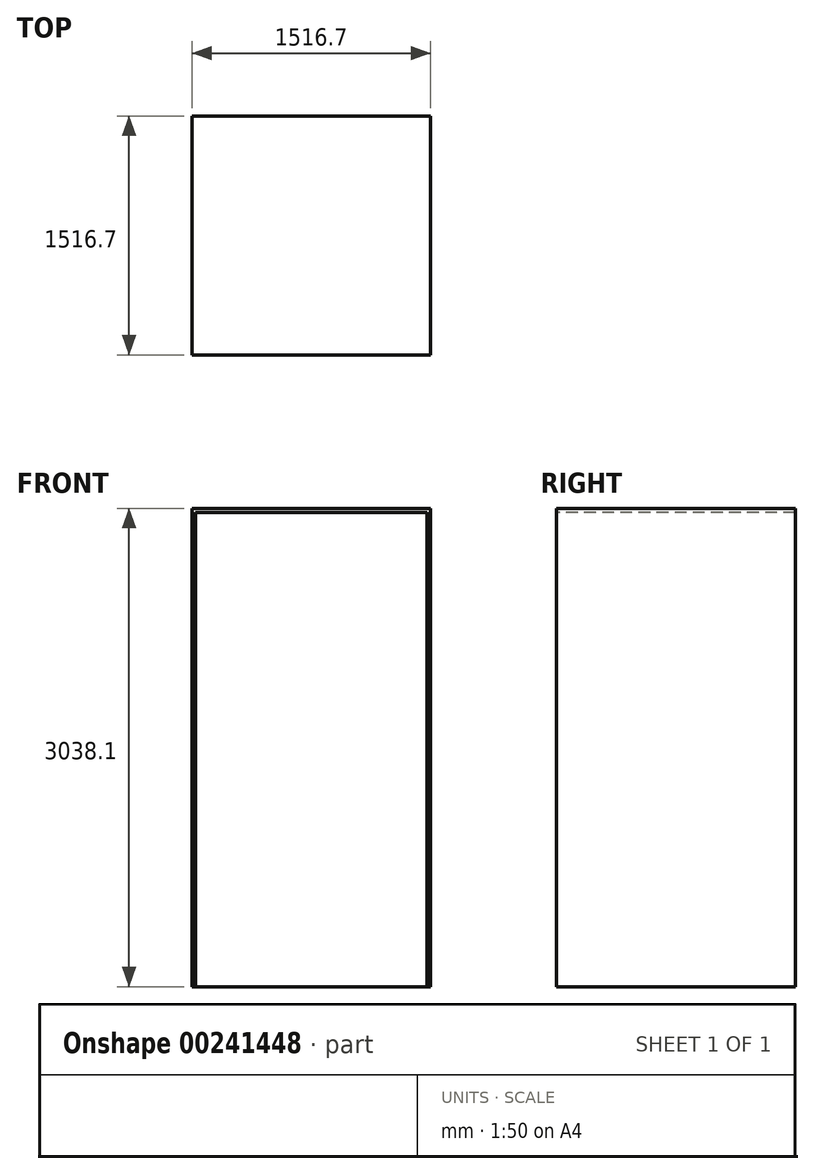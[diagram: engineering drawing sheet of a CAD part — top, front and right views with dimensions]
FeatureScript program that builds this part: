
annotation { "Feature Type Name" : "Feature", "Feature Type Description" : "" }
export const myFeature = defineFeature(function(context is Context, id is Id, definition is map)
    precondition{}
    {
        {
            var Q0;
            Q0=qCreatedBy(makeId("Top.planeOp"),FACE);
            var sketch = newSketch(context, id + "F0", { "sketchPlane" : qUnion([Q0])});
            skLineSegment(sketch, "E0.bottom", {"start": v(-758.35, 758.35) * mm, "end": v(758.35, 758.35) * mm});
            skLineSegment(sketch, "E0.top", {"start": v(-758.35, -758.35) * mm, "end": v(758.35, -758.35) * mm});
            skLineSegment(sketch, "E0.left", {"start": v(-758.35, 758.35) * mm, "end": v(-758.35, -758.35) * mm});
            skLineSegment(sketch, "E0.right", {"start": v(758.35, 758.35) * mm, "end": v(758.35, -758.35) * mm});
            skPoint(sketch, "E0.middle", {"position": v(0, 0) * mm});
            skLineSegment(sketch, "E1.bottom", {"start": v(-756.35, 756.35) * mm, "end": v(756.35, 756.35) * mm});
            skLineSegment(sketch, "E1.top", {"start": v(-756.35, -756.35) * mm, "end": v(756.35, -756.35) * mm});
            skLineSegment(sketch, "E1.left", {"start": v(-756.35, 756.35) * mm, "end": v(-756.35, -756.35) * mm});
            skLineSegment(sketch, "E1.right", {"start": v(756.35, 756.35) * mm, "end": v(756.35, -756.35) * mm});
            skSolve(sketch);
        }
        {
            var Q0;
            Q0=qCreatedBy(makeId("Front.planeOp"),FACE);
            var sketch = newSketch(context, id + "F1", { "sketchPlane" : qUnion([Q0])});
            skLineSegment(sketch, "E2", {"start": v(0, 0) * mm, "end": v(0, 166.97) * mm});
            skSolve(sketch);
        }
        {
            var Q0;
            Q0 = qSketchRegion(id + "F0", true);
            var Q1;
            Q1 = qSketchRegion(id + "F1", true);
            var Q2;
            Q2=sQuery(id+"F0.wireOp",EDGE,"E0.left");
            var Q3;
            Q3=sQuery(id+"F0.wireOp",EDGE,"E0.bottom");
            var Q4;
            Q4=sQuery(id+"F0.wireOp",EDGE,"E0.right");
            extrude(context, id + "F2", {"entities" : qUnion([Q0, Q1]), "surfaceEntities" : qUnion([Q2, Q3, Q4]), "depth" : 3012.7 * mm});
        }
        {
            var Q0;
            Q0=qCreatedBy(makeId("Top.planeOp"),FACE);
            cPlane(context, id + "F3", {"entities" : qUnion([Q0]), "cplaneType" : CPlaneType.OFFSET, "offset" : 3012.7 * mm, "width" : 150 * mm, "height" : 150 * mm});
        }
        {
            var Q0;
            Q0=qCreatedBy(id+"F3.planeOp",FACE);
            var sketch = newSketch(context, id + "F4", { "sketchPlane" : qUnion([Q0])});
            skLineSegment(sketch, "E3.bottom", {"start": v(-756.35, 756.35) * mm, "end": v(756.35, 756.35) * mm});
            skLineSegment(sketch, "E3.top", {"start": v(-756.35, -756.35) * mm, "end": v(756.35, -756.35) * mm});
            skLineSegment(sketch, "E3.left", {"start": v(-756.35, 756.35) * mm, "end": v(-756.35, -756.35) * mm});
            skLineSegment(sketch, "E3.right", {"start": v(756.35, 756.35) * mm, "end": v(756.35, -756.35) * mm});
            skPoint(sketch, "E3.middle", {"position": v(0, 0) * mm});
            skSolve(sketch);
        }
        {
            var Q0;
            Q0=qCreatedBy(makeId("Top.planeOp"),FACE);
            var sketch = newSketch(context, id + "F5", { "sketchPlane" : qUnion([Q0])});
            skLineSegment(sketch, "E4", {"start": v(-735.3, -756.35) * mm, "end": v(735.3, -756.35) * mm});
            skLineSegment(sketch, "E5", {"start": v(-735.3, -758.35) * mm, "end": v(735.3, -758.35) * mm});
            skLineSegment(sketch, "E6", {"start": v(-735.3, -758.35) * mm, "end": v(-735.3, -756.35) * mm});
            skLineSegment(sketch, "E7", {"start": v(735.3, -758.35) * mm, "end": v(735.3, -756.35) * mm});
            skSolve(sketch);
        }
        {
            var Q0;
            Q0 = qSketchRegion(id + "F5", true);
            extrude(context, id + "F6", {"entities" : qUnion([Q0]), "depth" : 3014.7 * mm});
        }
        {
            var Q0;
            Q0=makeQuery(id+"F6.opExtrude","SWEPT_BODY",BODY,{"disambiguationData":[OSD([sQuery(id+"F5.wireOp",EDGE,"E4"),sQuery(id+"F5.wireOp",EDGE,"E5"),sQuery(id+"F5.wireOp",EDGE,"E6"),sQuery(id+"F5.wireOp",EDGE,"E7")])]});
            var Q1;
            Q1=makeQuery(id+"F2.opExtrude","SWEPT_BODY",BODY,{"disambiguationData":[OSD([sQuery(id+"F0.wireOp",EDGE,"E0.bottom"),sQuery(id+"F0.wireOp",EDGE,"E0.top"),sQuery(id+"F0.wireOp",EDGE,"E0.left"),sQuery(id+"F0.wireOp",EDGE,"E0.right"),sQuery(id+"F0.wireOp",EDGE,"E1.bottom"),sQuery(id+"F0.wireOp",EDGE,"E1.top"),sQuery(id+"F0.wireOp",EDGE,"E1.left"),sQuery(id+"F0.wireOp",EDGE,"E1.right")])]});
            booleanBodies(context, id + "F7", {"operationType" : BooleanOperationType.SUBTRACTION, "tools" : qUnion([Q0]), "targets" : qUnion([Q1])});
        }
        {
            var Q0;
            Q0=qCreatedBy(id+"F3.planeOp",FACE);
            var sketch = newSketch(context, id + "F8", { "sketchPlane" : qUnion([Q0])});
            skLineSegment(sketch, "E8.bottom", {"start": v(-758.35, 758.35) * mm, "end": v(758.35, 758.35) * mm});
            skLineSegment(sketch, "E8.top", {"start": v(-758.35, -758.35) * mm, "end": v(758.35, -758.35) * mm});
            skLineSegment(sketch, "E8.left", {"start": v(-758.35, 758.35) * mm, "end": v(-758.35, -758.35) * mm});
            skLineSegment(sketch, "E8.right", {"start": v(758.35, 758.35) * mm, "end": v(758.35, -758.35) * mm});
            skPoint(sketch, "E8.middle", {"position": v(0, 0) * mm});
            skSolve(sketch);
        }
        {
            var Q0;
            Q0 = qSketchRegion(id + "F8", true);
            extrude(context, id + "F9", {"entities" : qUnion([Q0]), "operationType" : NewBodyOperationType.ADD, "depth" : 25.4 * mm});
        }
    });
